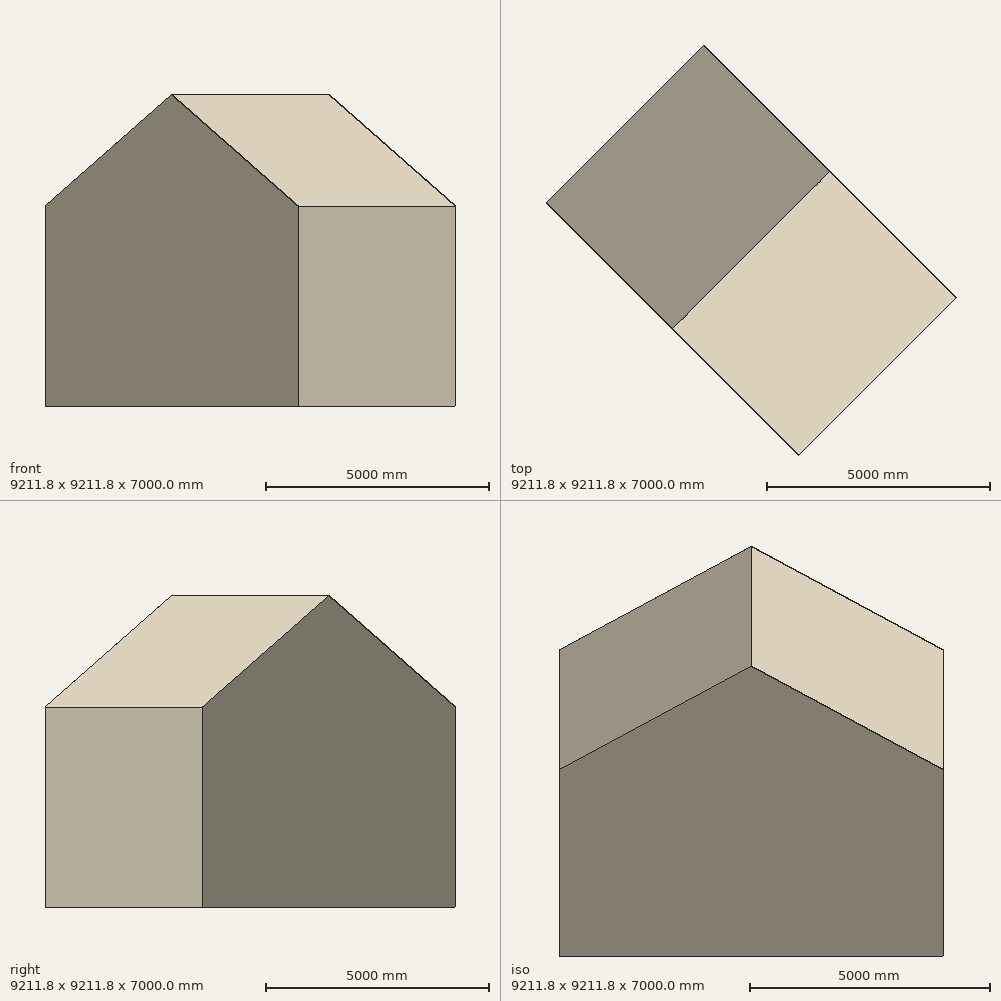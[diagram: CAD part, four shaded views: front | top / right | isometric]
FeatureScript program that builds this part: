
annotation { "Feature Type Name" : "Feature", "Feature Type Description" : "" }
export const myFeature = defineFeature(function(context is Context, id is Id, definition is map)
    precondition{}
    {
        {
            var Q0;
            Q0=qCreatedBy(makeId("Front.planeOp"),FACE);
            var sketch = newSketch(context, id + "F0", { "sketchPlane" : qUnion([Q0])});
            skLineSegment(sketch, "E0", {"start": v(0, 0) * mm, "end": v(0, 78.2) * mm, "construction": true});
            skLineSegment(sketch, "E1", {"start": v(0, 0) * mm, "end": v(-107.34, 0) * mm, "construction": true});
            skSolve(sketch);
        }
        {
            var Q0;
            Q0=qCreatedBy(makeId("Top.planeOp"),FACE);
            var sketch = newSketch(context, id + "F1", { "sketchPlane" : qUnion([Q0])});
            skLineSegment(sketch, "E2", {"start": v(0, 0) * mm, "end": v(-77.42, -77.42) * mm, "construction": true});
            skLineSegment(sketch, "E3", {"start": v(0, 0) * mm, "end": v(-57.52, 57.52) * mm, "construction": true});
            skSolve(sketch);
        }
        {
            var Q0;
            Q0=sQuery(id+"F0.wireOp",VERTEX,"E0.end");
            var Q1;
            Q1=sQuery(id+"F1.wireOp",VERTEX,"E2.start");
            var Q2;
            Q2=sQuery(id+"F1.wireOp",VERTEX,"E3.end");
            cPlane(context, id + "F2", {"entities" : qUnion([Q0, Q1, Q2]), "cplaneType" : CPlaneType.THREE_POINT, "offset" : 25 * mm, "width" : 150 * mm, "height" : 150 * mm});
        }
        {
            var Q0;
            Q0=qCreatedBy(id+"F2.planeOp",FACE);
            var sketch = newSketch(context, id + "F3", { "sketchPlane" : qUnion([Q0])});
            skLineSegment(sketch, "E4", {"start": v(0, 2500) * mm, "end": v(-4013.72, 0) * mm});
            skLineSegment(sketch, "E5", {"start": v(0, 2500) * mm, "end": v(0, 0) * mm, "construction": true});
            skLineSegment(sketch, "E6", {"start": v(-4013.72, 0) * mm, "end": v(-4013.72, -4500) * mm});
            skLineSegment(sketch, "E7.MirrorCS", {"start": v(0, 2500) * mm, "end": v(4013.72, 0) * mm});
            skLineSegment(sketch, "E8.MirrorCS", {"start": v(4013.72, 0) * mm, "end": v(4013.72, -4500) * mm});
            skLineSegment(sketch, "E9", {"start": v(4013.72, -4500) * mm, "end": v(-4013.72, -4500) * mm});
            skSolve(sketch);
        }
        {
            var Q0;
            Q0 = qSketchRegion(id + "F3", true);
            extrude(context, id + "F4", {"entities" : qUnion([Q0]), "endBound" : BoundingType.SYMMETRIC, "depth" : 5000 * mm});
        }
    });
